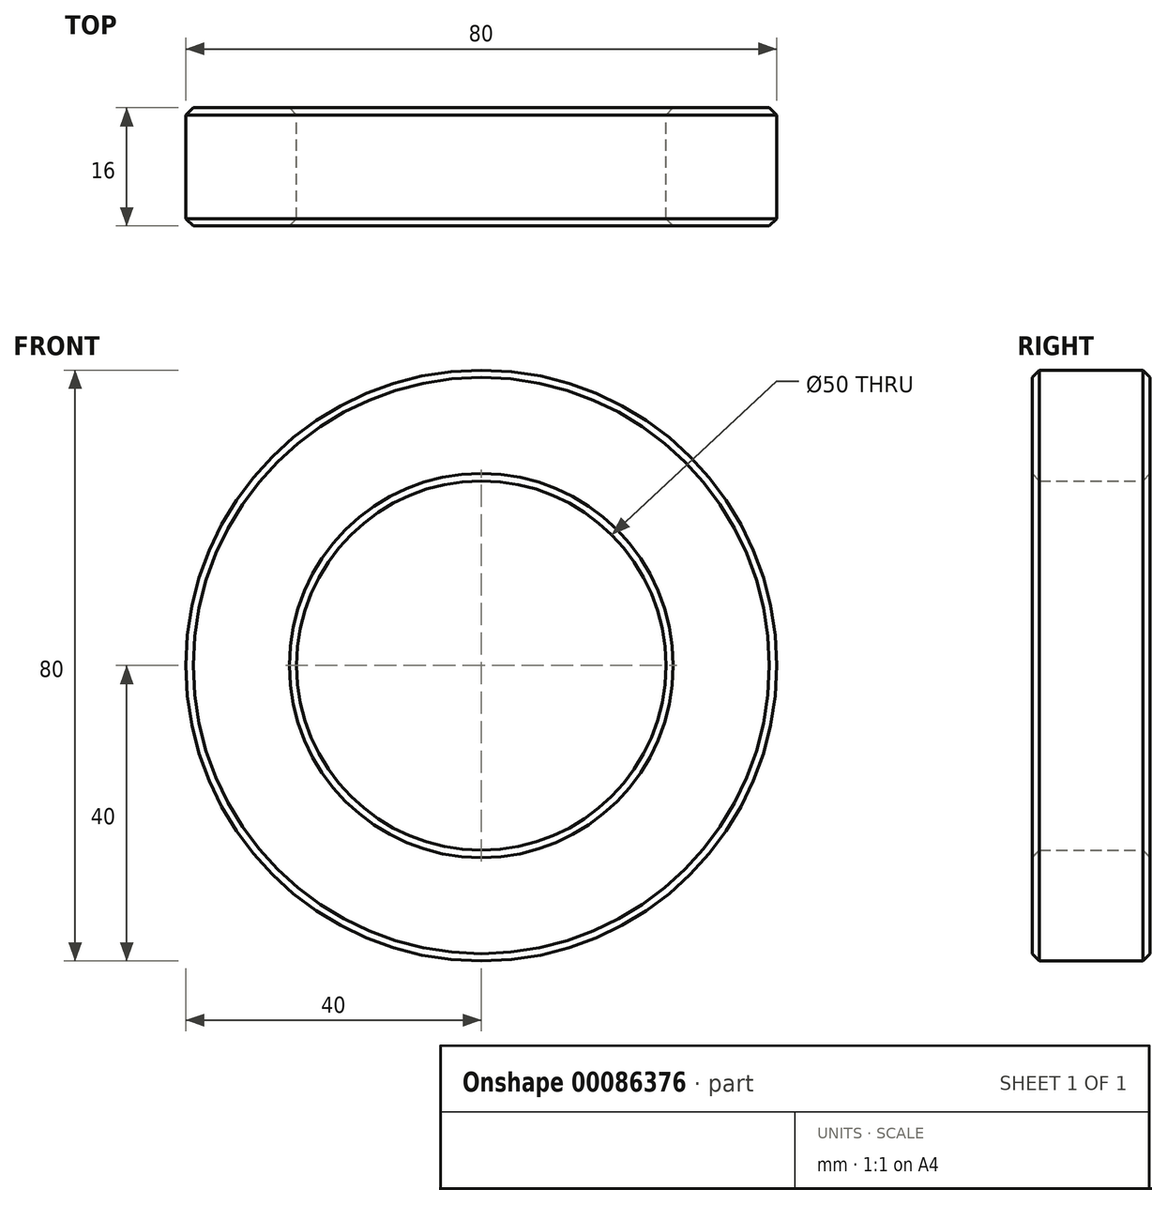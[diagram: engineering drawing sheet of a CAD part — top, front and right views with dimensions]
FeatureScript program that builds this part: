
annotation { "Feature Type Name" : "Feature", "Feature Type Description" : "" }
export const myFeature = defineFeature(function(context is Context, id is Id, definition is map)
    precondition{}
    {
        {
            var Q0;
            Q0=qCreatedBy(makeId("Front.planeOp"),FACE);
            var sketch = newSketch(context, id + "F0", { "sketchPlane" : qUnion([Q0])});
            skCircle(sketch, "E0", {"center": v(0, 0) * mm, "radius": 40 * mm});
            skCircle(sketch, "E1", {"center": v(0, 0) * mm, "radius": 25 * mm});
            skSolve(sketch);
        }
        {
            var Q0;
            Q0=qSketchRegion(id+"F0",true);
            extrude(context, id + "F1", {"entities" : qUnion([Q0]), "depth" : 16 * mm, "offsetDistance" : 25 * mm});
        }
        {
            var Q0;
            Q0=makeQuery(id+"F1.opExtrude","CAP_FACE",FACE,{"disambiguationData":[OSD([sQuery(id+"F0.wireOp",EDGE,"E0"),sQuery(id+"F0.wireOp",EDGE,"E1")])],"isStart":false});
            var Q1;
            Q1=makeQuery(id+"F1.opExtrude","CAP_FACE",FACE,{"disambiguationData":[OSD([sQuery(id+"F0.wireOp",EDGE,"E0"),sQuery(id+"F0.wireOp",EDGE,"E1")])],"isStart":true});
            chamfer(context, id + "F2", {"entities" : qUnion([Q0, Q1]), "width" : 1 * mm, "tangentPropagation" : true});
        }
    });
